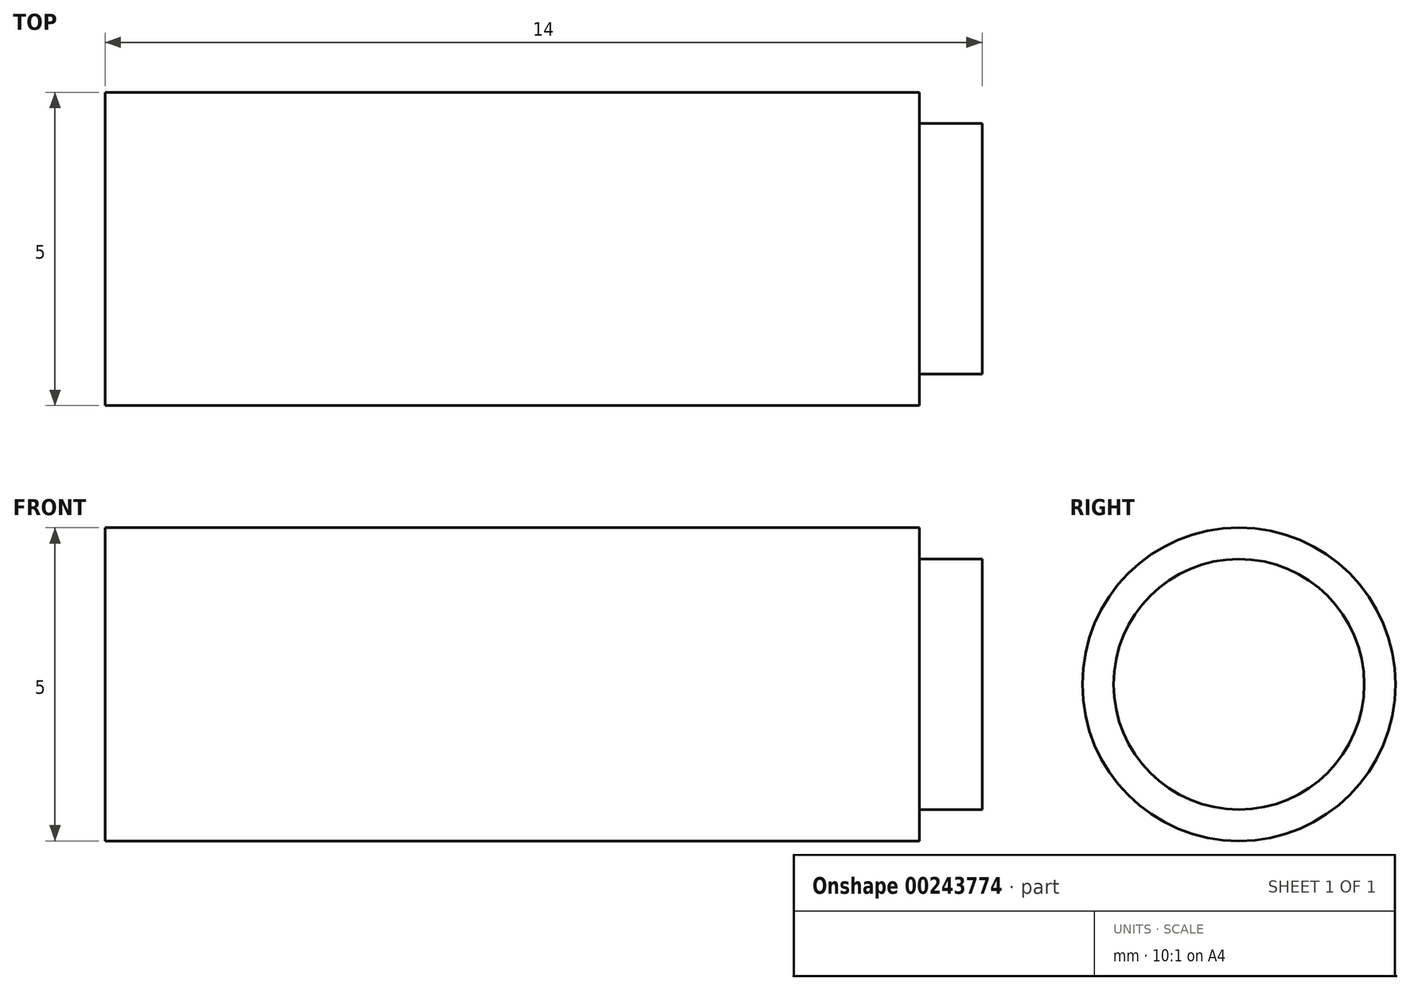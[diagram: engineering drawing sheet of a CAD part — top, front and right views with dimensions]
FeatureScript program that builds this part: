
annotation { "Feature Type Name" : "Feature", "Feature Type Description" : "" }
export const myFeature = defineFeature(function(context is Context, id is Id, definition is map)
    precondition{}
    {
        {
            var Q0;
            Q0=qCreatedBy(makeId("Front.planeOp"),FACE);
            var sketch = newSketch(context, id + "F0", { "sketchPlane" : qUnion([Q0])});
            skLineSegment(sketch, "E0", {"start": v(0, 2) * mm, "end": v(-1, 2) * mm});
            skLineSegment(sketch, "E1", {"start": v(-1, 2) * mm, "end": v(-1, 2.5) * mm});
            skLineSegment(sketch, "E2", {"start": v(-1, 2.5) * mm, "end": v(-14, 2.5) * mm});
            skLineSegment(sketch, "E3", {"start": v(-14, 2.5) * mm, "end": v(-14, 0) * mm});
            skLineSegment(sketch, "E4", {"start": v(-14, 0) * mm, "end": v(0, 0) * mm});
            skLineSegment(sketch, "E5", {"start": v(0, 0) * mm, "end": v(0, 2) * mm});
            skLineSegment(sketch, "E6", {"start": v(-16.35, 0) * mm, "end": v(2.22, 0) * mm, "construction": true});
            skSolve(sketch);
        }
        {
            var Q0;
            Q0=makeQuery(id+"F0.imprint","IMPRINT",FACE,{"disambiguationData":[TD([[makeQuery(id+"F0.imprint","IMPRINT",EDGE,{"derivedFrom":sQuery(id+"F0.wireOp",EDGE,"E0")}),1.0]])]});
            var Q1;
            Q1=sQuery(id+"F0.wireOp",EDGE,"E6");
            revolve(context, id + "F1", {"entities" : qUnion([Q0]), "axis" : qUnion([Q1]), "revolveType" : RevolveType.FULL});
        }
    });
